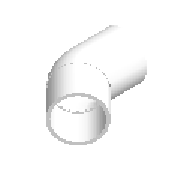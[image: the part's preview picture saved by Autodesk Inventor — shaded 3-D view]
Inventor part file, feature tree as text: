
AUTODESK INVENTOR PART (.ipt)
format: ipt  version: 2023 (Build 270158000, 158)  size: 262,144 bytes
history: native  units: mm (DEFAULTED — no unit token found)
features: revolve x6, other x6, sketch x3
ambient origin geometry x8: Origin, YZ Plane, XZ Plane, XY Plane, X Axis, Y Axis, Z Axis, Center Point
bodies: Solid1 (feature_tree)
feature tree (15):
  sketch  "Sketch1"  dims[d0=86.0mm d1=34.0mm]
  revolve  "Revolution1"  [1 undecoded]
  revolve  "Revolution2"  [1 undecoded]
  revolve  "Revolution3"  [1 undecoded]
  revolve  "Revolution4"  Angle=135.0deg
  sketch  "Sketch2"  dims[d2=160.0mm d3=11.9mm]
  revolve  "Revolution5"  Angle=90.0deg
  revolve  "Revolution6"  Angle=90.0deg
  other  "Work Point1"
  other  "Work Point2"
  other  "Work Axis1"
  other  "Work Point3"
  other  "Work Axis2"
  other  "Work Point4"
  sketch  "Sketch3"  dims[d4=11.9mm d5=160.0mm d6=135.0deg d139=90.0deg d140=90.0deg d7=86.0mm d8=34.0mm d9=5.78mm d10=5.78mm d11=152.0mm d203=7.845255mm d12=152.0mm d205=7.845255mm d13=152.0mm d14=183.8mm d15=0.01mm d16=45.0deg d17=8.0mm d18=320.0mm d19=45.0deg]
note: 3 required parameter values undecoded (feature->parameter linkage not recoverable at this tier; creation-order binding heuristic only, values carry confidence <= 0.55)
